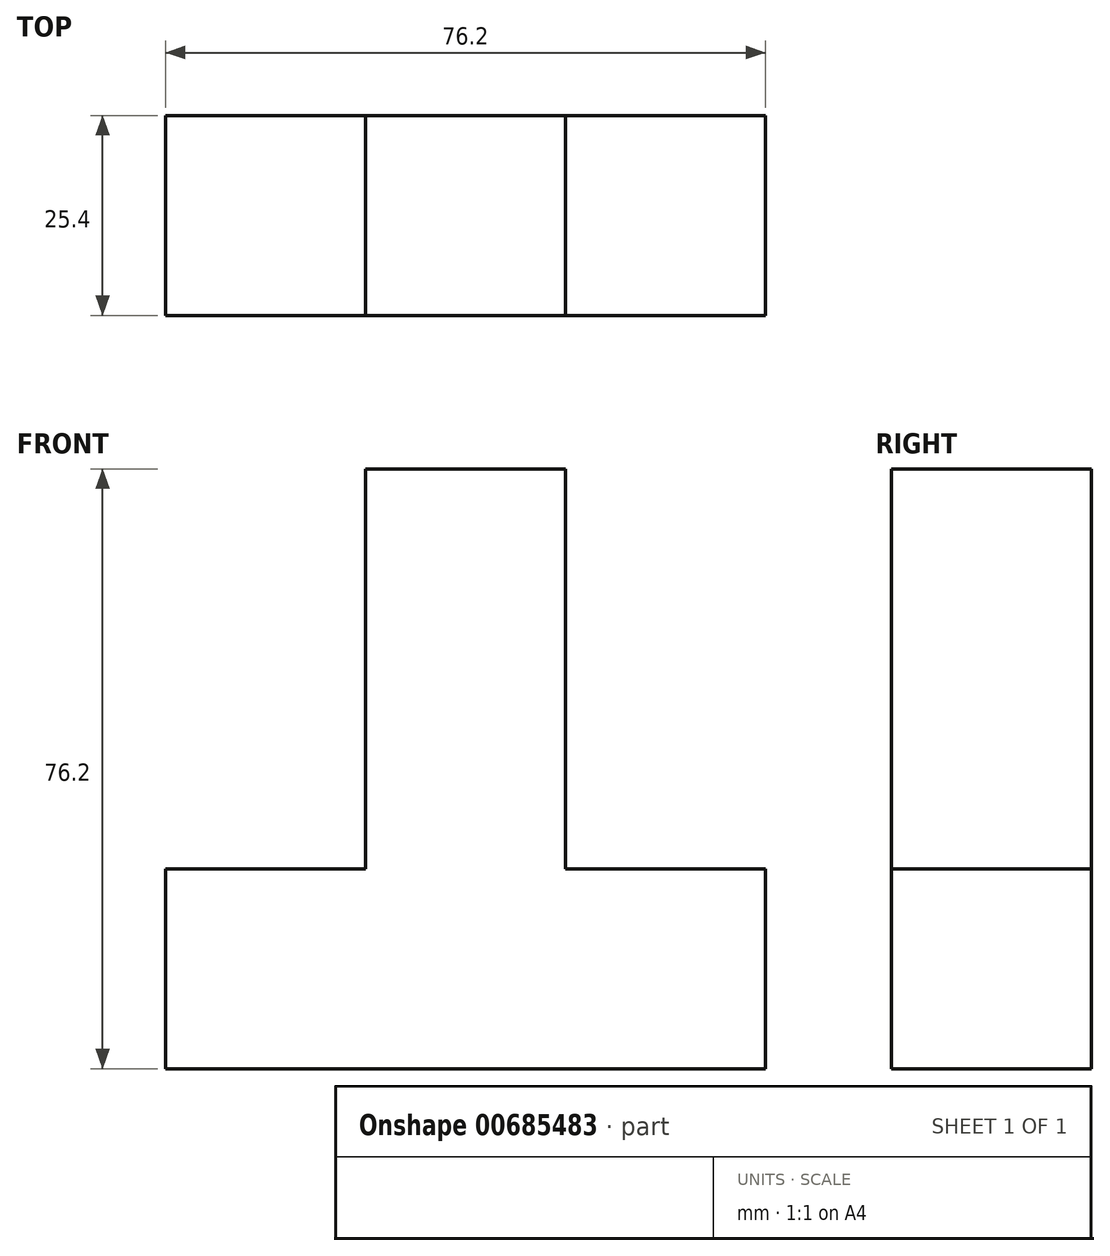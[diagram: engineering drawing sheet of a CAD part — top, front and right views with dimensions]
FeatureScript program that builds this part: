
annotation { "Feature Type Name" : "Feature", "Feature Type Description" : "" }
export const myFeature = defineFeature(function(context is Context, id is Id, definition is map)
    precondition{}
    {
        {
            var Q0;
            Q0=qCreatedBy(makeId("Front.planeOp"),FACE);
            var sketch = newSketch(context, id + "F0", { "sketchPlane" : qUnion([Q0])});
            skLineSegment(sketch, "E0", {"start": v(-22.84, 0) * mm, "end": v(53.36, 0) * mm});
            skLineSegment(sketch, "E1", {"start": v(53.36, 0) * mm, "end": v(53.36, 25.4) * mm});
            skLineSegment(sketch, "E2", {"start": v(53.36, 25.4) * mm, "end": v(27.96, 25.4) * mm});
            skLineSegment(sketch, "E3", {"start": v(27.96, 25.4) * mm, "end": v(27.96, 76.2) * mm});
            skLineSegment(sketch, "E4", {"start": v(-22.84, 0) * mm, "end": v(-22.84, 25.4) * mm});
            skLineSegment(sketch, "E5", {"start": v(-22.84, 25.4) * mm, "end": v(2.56, 25.4) * mm});
            skLineSegment(sketch, "E6", {"start": v(2.56, 25.4) * mm, "end": v(2.56, 76.2) * mm});
            skLineSegment(sketch, "E7", {"start": v(2.56, 76.2) * mm, "end": v(27.96, 76.2) * mm});
            skSolve(sketch);
        }
        {
            var Q0;
            Q0 = qSketchRegion(id + "F0", true);
            extrude(context, id + "F1", {"entities" : qUnion([Q0]), "depth" : 25.4 * mm, "offsetDistance" : 25.4 * mm});
        }
    });
